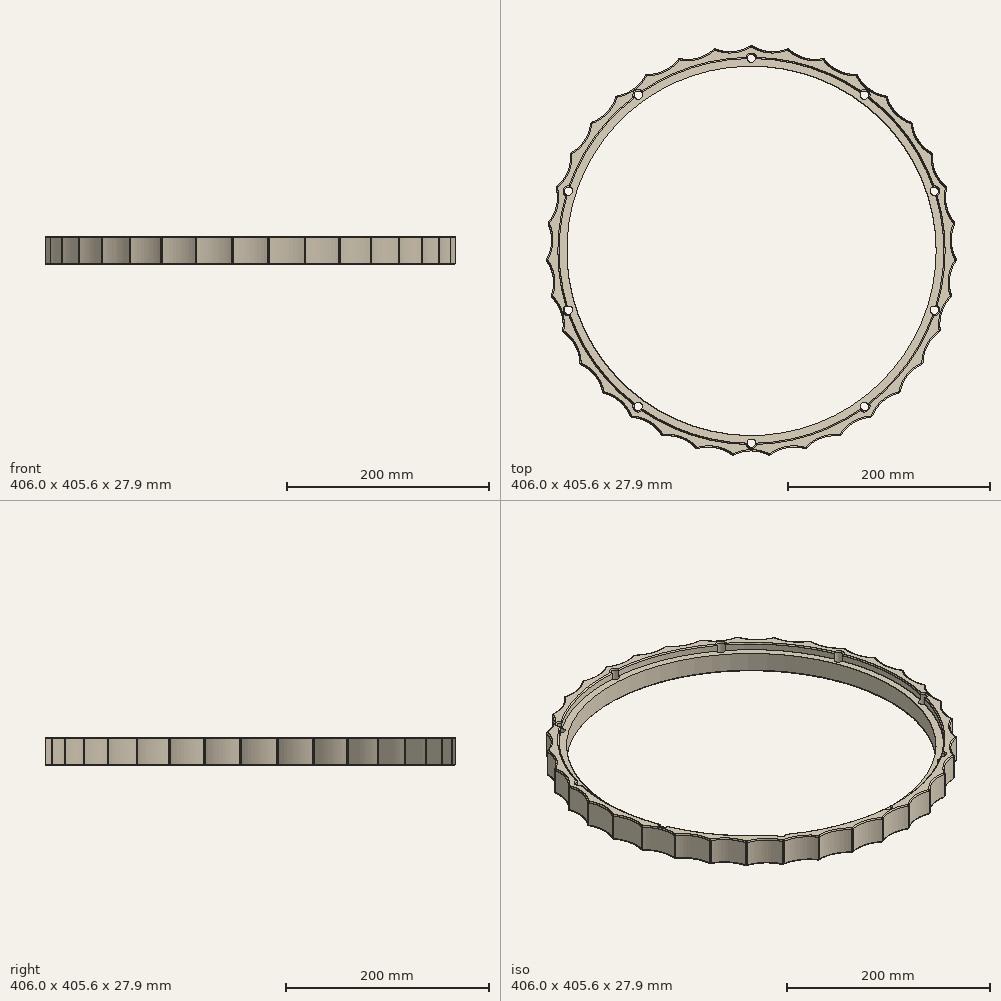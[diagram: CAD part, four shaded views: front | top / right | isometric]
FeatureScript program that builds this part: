
annotation { "Feature Type Name" : "Feature", "Feature Type Description" : "" }
export const myFeature = defineFeature(function(context is Context, id is Id, definition is map)
    precondition{}
    {
        {
            var Q0;
            Q0=qCreatedBy(makeId("Top.planeOp"),FACE);
            var sketch = newSketch(context, id + "F0", { "sketchPlane" : qUnion([Q0])});
            skCircle(sketch, "E0", {"center": v(0, 0) * mm, "radius": 182.88 * mm});
            skCircle(sketch, "E1", {"center": v(0, 0) * mm, "radius": 203.2 * mm});
            skSolve(sketch);
        }
        {
            var Q0;
            Q0=makeQuery(id+"F0.imprint","IMPRINT",FACE,{"disambiguationData":[TD([[makeQuery(id+"F0.imprint","IMPRINT",EDGE,{"derivedFrom":sQuery(id+"F0.wireOp",EDGE,"E0")}),-1.0]])]});
            extrude(context, id + "F1", {"entities" : qUnion([Q0]), "depth" : 27.94 * mm, "offsetDistance" : 25.4 * mm});
        }
        {
            var Q0;
            Q0=qCreatedBy(makeId("Top.planeOp"),FACE);
            var sketch = newSketch(context, id + "F2", { "sketchPlane" : qUnion([Q0])});
            skArc(sketch, "E2", {"start": v(-23.93, -265.87) * mm, "mid": v(0, -274.32) * mm, "end": v(23.93, -265.87) * mm});
            skArc(sketch, "E3.1.0", {"start": v(23.93, -265.87) * mm, "mid": v(48.98, -269.91) * mm, "end": v(71.02, -257.32) * mm});
            skArc(sketch, "E3.2.0", {"start": v(71.02, -257.32) * mm, "mid": v(96.39, -256.83) * mm, "end": v(115.82, -240.5) * mm});
            skArc(sketch, "E3.3.0", {"start": v(115.82, -240.5) * mm, "mid": v(140.7, -235.49) * mm, "end": v(156.9, -215.96) * mm});
            skArc(sketch, "E3.4.0", {"start": v(156.9, -215.96) * mm, "mid": v(180.49, -206.58) * mm, "end": v(192.95, -184.47) * mm});
            skArc(sketch, "E3.5.0", {"start": v(192.95, -184.47) * mm, "mid": v(214.47, -171.04) * mm, "end": v(222.78, -147.06) * mm});
            skArc(sketch, "E3.6.0", {"start": v(222.78, -147.06) * mm, "mid": v(241.56, -130) * mm, "end": v(245.46, -104.92) * mm});
            skArc(sketch, "E3.7.0", {"start": v(245.46, -104.92) * mm, "mid": v(260.9, -84.77) * mm, "end": v(260.25, -59.4) * mm});
            skArc(sketch, "E3.8.0", {"start": v(260.25, -59.4) * mm, "mid": v(271.84, -36.82) * mm, "end": v(266.67, -11.98) * mm});
            skArc(sketch, "E3.9.0", {"start": v(201.75, 27.33) * mm, "mid": v(197.92, 8.89) * mm, "end": v(203.39, -9.13) * mm});
            skArc(sketch, "E3.10.0", {"start": v(193.63, 62.91) * mm, "mid": v(193.15, 44.09) * mm, "end": v(201.75, 27.33) * mm});
            skArc(sketch, "E3.11.0", {"start": v(179.28, 96.48) * mm, "mid": v(182.18, 77.87) * mm, "end": v(193.63, 62.91) * mm});
            skArc(sketch, "E3.12.0", {"start": v(235.07, 126.5) * mm, "mid": v(228.94, 151.12) * mm, "end": v(208.7, 166.44) * mm});
            skArc(sketch, "E3.13.0", {"start": v(208.7, 166.44) * mm, "mid": v(198.28, 189.57) * mm, "end": v(175.63, 201.03) * mm});
            skArc(sketch, "E3.14.0", {"start": v(104.42, 174.78) * mm, "mid": v(116.45, 160.28) * mm, "end": v(133.95, 153.32) * mm});
            skArc(sketch, "E3.15.0", {"start": v(136.91, 229.16) * mm, "mid": v(119.02, 247.15) * mm, "end": v(93.8, 249.92) * mm});
            skArc(sketch, "E3.16.0", {"start": v(93.8, 249.92) * mm, "mid": v(72.98, 264.43) * mm, "end": v(47.66, 262.65) * mm});
            skArc(sketch, "E3.17.0", {"start": v(47.66, 262.65) * mm, "mid": v(24.59, 273.22) * mm, "end": v(0, 266.94) * mm});
            skArc(sketch, "E3.18.0", {"start": v(-36.35, 200.32) * mm, "mid": v(-17.76, 197.32) * mm, "end": v(0, 203.6) * mm});
            skArc(sketch, "E3.19.0", {"start": v(-47.66, 262.65) * mm, "mid": v(-72.98, 264.43) * mm, "end": v(-93.8, 249.92) * mm});
            skArc(sketch, "E3.20.0", {"start": v(-104.42, 174.78) * mm, "mid": v(-85.96, 178.5) * mm, "end": v(-71.54, 190.61) * mm});
            skArc(sketch, "E3.21.0", {"start": v(-136.91, 229.16) * mm, "mid": v(-161.24, 221.93) * mm, "end": v(-175.63, 201.03) * mm});
            skArc(sketch, "E3.22.0", {"start": v(-175.63, 201.03) * mm, "mid": v(-198.28, 189.57) * mm, "end": v(-208.7, 166.44) * mm});
            skArc(sketch, "E3.23.0", {"start": v(-179.28, 96.48) * mm, "mid": v(-165.35, 109.14) * mm, "end": v(-159.18, 126.94) * mm});
            skArc(sketch, "E3.24.0", {"start": v(-193.63, 62.91) * mm, "mid": v(-182.18, 77.87) * mm, "end": v(-179.28, 96.48) * mm});
            skArc(sketch, "E3.25.0", {"start": v(-201.75, 27.33) * mm, "mid": v(-193.15, 44.09) * mm, "end": v(-193.63, 62.91) * mm});
            skArc(sketch, "E3.26.0", {"start": v(-203.39, -9.13) * mm, "mid": v(-197.92, 8.89) * mm, "end": v(-201.75, 27.33) * mm});
            skArc(sketch, "E3.27.0", {"start": v(-266.67, -11.98) * mm, "mid": v(-271.84, -36.82) * mm, "end": v(-260.25, -59.4) * mm});
            skArc(sketch, "E3.28.0", {"start": v(-260.25, -59.4) * mm, "mid": v(-260.9, -84.77) * mm, "end": v(-245.46, -104.92) * mm});
            skArc(sketch, "E3.29.0", {"start": v(-245.46, -104.92) * mm, "mid": v(-241.56, -130) * mm, "end": v(-222.78, -147.06) * mm});
            skArc(sketch, "E3.30.0", {"start": v(-222.78, -147.06) * mm, "mid": v(-214.47, -171.04) * mm, "end": v(-192.95, -184.47) * mm});
            skArc(sketch, "E3.31.0", {"start": v(-192.95, -184.47) * mm, "mid": v(-180.49, -206.58) * mm, "end": v(-156.9, -215.96) * mm});
            skArc(sketch, "E3.32.0", {"start": v(-156.9, -215.96) * mm, "mid": v(-140.7, -235.49) * mm, "end": v(-115.82, -240.5) * mm});
            skArc(sketch, "E3.33.0", {"start": v(-115.82, -240.5) * mm, "mid": v(-96.39, -256.83) * mm, "end": v(-71.02, -257.32) * mm});
            skArc(sketch, "E3.34.0", {"start": v(-71.02, -257.32) * mm, "mid": v(-48.98, -269.91) * mm, "end": v(-23.93, -265.87) * mm});
            skPoint(sketch, "E3.center", {"position": v(0, 0) * mm});
            skArc(sketch, "E4.trimOffspring", {"start": v(0, 266.94) * mm, "mid": v(-24.59, 273.22) * mm, "end": v(-47.66, 262.65) * mm});
            skArc(sketch, "E5.trimOffspring", {"start": v(36.35, 200.32) * mm, "mid": v(52.7, 190.98) * mm, "end": v(71.54, 190.61) * mm});
            skArc(sketch, "E6.trimOffspring", {"start": v(0, 203.6) * mm, "mid": v(17.76, 197.32) * mm, "end": v(36.35, 200.32) * mm});
            skArc(sketch, "E7.trimOffspring", {"start": v(71.54, 190.61) * mm, "mid": v(85.96, 178.5) * mm, "end": v(104.42, 174.78) * mm});
            skArc(sketch, "E8.trimOffspring", {"start": v(-133.95, 153.32) * mm, "mid": v(-116.45, 160.28) * mm, "end": v(-104.42, 174.78) * mm});
            skArc(sketch, "E9.trimOffspring", {"start": v(-71.54, 190.61) * mm, "mid": v(-52.7, 190.98) * mm, "end": v(-36.35, 200.32) * mm});
            skArc(sketch, "E10.trimOffspring", {"start": v(-93.8, 249.92) * mm, "mid": v(-119.02, 247.15) * mm, "end": v(-136.91, 229.16) * mm});
            skArc(sketch, "E11.trimOffspring", {"start": v(253.88, 82.49) * mm, "mid": v(252.24, 107.81) * mm, "end": v(235.07, 126.5) * mm});
            skArc(sketch, "E12.trimOffspring", {"start": v(159.18, 126.94) * mm, "mid": v(165.35, 109.14) * mm, "end": v(179.28, 96.48) * mm});
            skArc(sketch, "E13.trimOffspring", {"start": v(175.63, 201.03) * mm, "mid": v(161.24, 221.93) * mm, "end": v(136.91, 229.16) * mm});
            skArc(sketch, "E14.trimOffspring", {"start": v(133.95, 153.32) * mm, "mid": v(143.2, 136.91) * mm, "end": v(159.18, 126.94) * mm});
            skArc(sketch, "E15.trimOffspring", {"start": v(-264.53, 35.83) * mm, "mid": v(-274.04, 12.3) * mm, "end": v(-266.67, -11.98) * mm});
            skArc(sketch, "E16.trimOffspring", {"start": v(-253.88, 82.49) * mm, "mid": v(-267.44, 61.04) * mm, "end": v(-264.53, 35.83) * mm});
            skArc(sketch, "E17.trimOffspring", {"start": v(-235.07, 126.5) * mm, "mid": v(-252.24, 107.81) * mm, "end": v(-253.88, 82.49) * mm});
            skArc(sketch, "E18.trimOffspring", {"start": v(-159.18, 126.94) * mm, "mid": v(-143.2, 136.91) * mm, "end": v(-133.95, 153.32) * mm});
            skArc(sketch, "E19.trimOffspring", {"start": v(-208.7, 166.44) * mm, "mid": v(-228.94, 151.12) * mm, "end": v(-235.07, 126.5) * mm});
            skArc(sketch, "E20.trimOffspring", {"start": v(-198.5, -45.3) * mm, "mid": v(-196.33, -26.6) * mm, "end": v(-203.39, -9.13) * mm});
            skArc(sketch, "E21.trimOffspring", {"start": v(-187.21, -80.02) * mm, "mid": v(-188.42, -61.22) * mm, "end": v(-198.5, -45.3) * mm});
            skArc(sketch, "E22.trimOffspring", {"start": v(-169.91, -112.16) * mm, "mid": v(-174.46, -93.88) * mm, "end": v(-187.21, -80.02) * mm});
            skArc(sketch, "E23.trimOffspring", {"start": v(-147.16, -140.7) * mm, "mid": v(-154.9, -123.53) * mm, "end": v(-169.91, -112.16) * mm});
            skArc(sketch, "E24.trimOffspring", {"start": v(-119.67, -164.71) * mm, "mid": v(-130.35, -149.2) * mm, "end": v(-147.16, -140.7) * mm});
            skArc(sketch, "E25.trimOffspring", {"start": v(-88.34, -183.43) * mm, "mid": v(-101.62, -170.08) * mm, "end": v(-119.67, -164.71) * mm});
            skArc(sketch, "E26.trimOffspring", {"start": v(-54.16, -196.26) * mm, "mid": v(-69.61, -185.49) * mm, "end": v(-88.34, -183.43) * mm});
            skArc(sketch, "E27.trimOffspring", {"start": v(-18.25, -202.78) * mm, "mid": v(-35.38, -194.94) * mm, "end": v(-54.16, -196.26) * mm});
            skArc(sketch, "E28.trimOffspring", {"start": v(18.25, -202.78) * mm, "mid": v(0, -198.12) * mm, "end": v(-18.25, -202.78) * mm});
            skArc(sketch, "E29.trimOffspring", {"start": v(54.16, -196.26) * mm, "mid": v(35.38, -194.94) * mm, "end": v(18.25, -202.78) * mm});
            skArc(sketch, "E30.trimOffspring", {"start": v(88.34, -183.43) * mm, "mid": v(69.61, -185.49) * mm, "end": v(54.16, -196.26) * mm});
            skArc(sketch, "E31.trimOffspring", {"start": v(119.67, -164.71) * mm, "mid": v(101.62, -170.08) * mm, "end": v(88.34, -183.43) * mm});
            skArc(sketch, "E32.trimOffspring", {"start": v(147.16, -140.7) * mm, "mid": v(130.35, -149.2) * mm, "end": v(119.67, -164.71) * mm});
            skArc(sketch, "E33.trimOffspring", {"start": v(169.91, -112.16) * mm, "mid": v(154.9, -123.53) * mm, "end": v(147.16, -140.7) * mm});
            skArc(sketch, "E34.trimOffspring", {"start": v(187.21, -80.02) * mm, "mid": v(174.46, -93.88) * mm, "end": v(169.91, -112.16) * mm});
            skArc(sketch, "E35.trimOffspring", {"start": v(198.5, -45.3) * mm, "mid": v(188.42, -61.22) * mm, "end": v(187.21, -80.02) * mm});
            skArc(sketch, "E36.trimOffspring", {"start": v(266.67, -11.98) * mm, "mid": v(274.04, 12.3) * mm, "end": v(264.53, 35.83) * mm});
            skArc(sketch, "E37.trimOffspring", {"start": v(203.39, -9.13) * mm, "mid": v(196.33, -26.6) * mm, "end": v(198.5, -45.3) * mm});
            skArc(sketch, "E38.trimOffspring", {"start": v(264.53, 35.83) * mm, "mid": v(267.44, 61.04) * mm, "end": v(253.88, 82.49) * mm});
            skSolve(sketch);
        }
        {
            var Q0;
            Q0=makeQuery(id+"F2.imprint","IMPRINT",FACE,{"disambiguationData":[TD([[makeQuery(id+"F2.imprint","IMPRINT",EDGE,{"derivedFrom":sQuery(id+"F2.wireOp",EDGE,"E2")}),1.0]])]});
            extrude(context, id + "F3", {"entities" : qUnion([Q0]), "operationType" : NewBodyOperationType.REMOVE, "depth" : 50.8 * mm, "offsetDistance" : 25.4 * mm});
        }
        {
            var Q0;
            Q0=qCreatedBy(makeId("Top.planeOp"),FACE);
            var sketch = newSketch(context, id + "F4", { "sketchPlane" : qUnion([Q0])});
            skPoint(sketch, "E39", {"position": v(0, 190.5) * mm});
            skPoint(sketch, "E40.1.0", {"position": v(-111.97, 154.12) * mm});
            skPoint(sketch, "E40.2.0", {"position": v(-181.18, 58.87) * mm});
            skPoint(sketch, "E40.3.0", {"position": v(-181.18, -58.87) * mm});
            skPoint(sketch, "E40.4.0", {"position": v(-111.97, -154.12) * mm});
            skPoint(sketch, "E40.5.0", {"position": v(0, -190.5) * mm});
            skPoint(sketch, "E40.6.0", {"position": v(111.97, -154.12) * mm});
            skPoint(sketch, "E40.7.0", {"position": v(181.18, -58.87) * mm});
            skPoint(sketch, "E40.8.0", {"position": v(181.18, 58.87) * mm});
            skPoint(sketch, "E40.9.0", {"position": v(111.97, 154.12) * mm});
            skPoint(sketch, "E40.center", {"position": v(0, 0) * mm});
            skSolve(sketch);
        }
        {
            var Q0;
            Q0=sQuery(id+"F4.wireOp",VERTEX,"E40.2.0");
            var Q1;
            Q1=sQuery(id+"F4.wireOp",VERTEX,"E40.3.0");
            var Q2;
            Q2=sQuery(id+"F4.wireOp",VERTEX,"E40.4.0");
            var Q3;
            Q3=sQuery(id+"F4.wireOp",VERTEX,"E40.5.0");
            var Q4;
            Q4=sQuery(id+"F4.wireOp",VERTEX,"E40.6.0");
            var Q5;
            Q5=sQuery(id+"F4.wireOp",VERTEX,"E40.7.0");
            var Q6;
            Q6=sQuery(id+"F4.wireOp",VERTEX,"E40.8.0");
            var Q7;
            Q7=sQuery(id+"F4.wireOp",VERTEX,"E40.9.0");
            var Q8;
            Q8=sQuery(id+"F4.wireOp",VERTEX,"E39");
            var Q9;
            Q9=sQuery(id+"F4.wireOp",VERTEX,"E40.1.0");
            var Q10;
            Q10=makeQuery(id+"F1.opExtrude","SWEPT_BODY",BODY,{"disambiguationData":[OSD([sQuery(id+"F0.wireOp",EDGE,"E0"),sQuery(id+"F0.wireOp",EDGE,"E1")])]});
            hole(context, id + "F5", {"style" : HoleStyle.C_BORE, "endStyle" : HoleEndStyle.BLIND, "oppositeDirection" : true, "holeDiameter" : 8.43 * mm, "cBoreDiameter" : 12.7 * mm, "cBoreDepth" : 10.16 * mm, "majorDiameter" : 25.4 * mm, "holeDepth" : 50.8 * mm, "isTappedThrough" : true, "tappedDepth" : 6.35 * mm, "tapClearance" : 3, "startFromSketch" : true, "locations" : qUnion([Q0, Q1, Q2, Q3, Q4, Q5, Q6, Q7, Q8, Q9]), "scope" : qUnion([Q10])});
        }
        {
            var Q0;
            Q0=qCreatedBy(makeId("Front.planeOp"),FACE);
            var sketch = newSketch(context, id + "F6", { "sketchPlane" : qUnion([Q0])});
            skLineSegment(sketch, "E41.bottom", {"start": v(190.5, 20.32) * mm, "end": v(165.1, 20.32) * mm});
            skLineSegment(sketch, "E41.top", {"start": v(190.5, 45.72) * mm, "end": v(165.1, 45.72) * mm});
            skLineSegment(sketch, "E41.left", {"start": v(190.5, 20.32) * mm, "end": v(190.5, 45.72) * mm});
            skLineSegment(sketch, "E41.right", {"start": v(165.1, 20.32) * mm, "end": v(165.1, 45.72) * mm});
            skLineSegment(sketch, "E42", {"start": v(0, 0) * mm, "end": v(0, -266.52) * mm, "construction": true});
            skSolve(sketch);
        }
        {
            var Q0;
            Q0=makeQuery(id+"F6.imprint","IMPRINT",FACE,{"disambiguationData":[TD([[makeQuery(id+"F6.imprint","IMPRINT",EDGE,{"derivedFrom":sQuery(id+"F6.wireOp",EDGE,"E41.bottom")}),-1.0]])]});
            var Q1;
            Q1=sQuery(id+"F6.wireOp",EDGE,"E42");
            revolve(context, id + "F7", {"operationType" : NewBodyOperationType.REMOVE, "surfaceOperationType" : NewSurfaceOperationType.NEW, "entities" : qUnion([Q0]), "axis" : qUnion([Q1]), "revolveType" : RevolveType.FULL, "oppositeDirection" : true});
        }
        {
            var Q0;
            Q0=makeQuery(id+"F3.boolean.opBoolean","COPY",FACE,{"derivedFrom":makeQuery(id+"F3.opExtrude","SWEPT_FACE",FACE,{"disambiguationData":[OSD([sQuery(id+"F2.wireOp",EDGE,"E3.24.0")])]})});
            var Q1;
            Q1=makeQuery(id+"F3.boolean.opBoolean","COPY",FACE,{"derivedFrom":makeQuery(id+"F3.opExtrude","SWEPT_FACE",FACE,{"disambiguationData":[OSD([sQuery(id+"F2.wireOp",EDGE,"E3.23.0")])]})});
            var Q2;
            Q2=makeQuery(id+"F3.boolean.opBoolean","COPY",FACE,{"derivedFrom":makeQuery(id+"F3.opExtrude","SWEPT_FACE",FACE,{"disambiguationData":[OSD([sQuery(id+"F2.wireOp",EDGE,"E18.trimOffspring")])]})});
            var Q3;
            Q3=makeQuery(id+"F3.boolean.opBoolean","COPY",FACE,{"derivedFrom":makeQuery(id+"F3.opExtrude","SWEPT_FACE",FACE,{"disambiguationData":[OSD([sQuery(id+"F2.wireOp",EDGE,"E8.trimOffspring")])]})});
            var Q4;
            Q4=makeQuery(id+"F3.boolean.opBoolean","COPY",FACE,{"derivedFrom":makeQuery(id+"F3.opExtrude","SWEPT_FACE",FACE,{"disambiguationData":[OSD([sQuery(id+"F2.wireOp",EDGE,"E3.20.0")])]})});
            var Q5;
            Q5=makeQuery(id+"F3.boolean.opBoolean","COPY",FACE,{"derivedFrom":makeQuery(id+"F3.opExtrude","SWEPT_FACE",FACE,{"disambiguationData":[OSD([sQuery(id+"F2.wireOp",EDGE,"E9.trimOffspring")])]})});
            var Q6;
            Q6=makeQuery(id+"F3.boolean.opBoolean","COPY",FACE,{"derivedFrom":makeQuery(id+"F3.opExtrude","SWEPT_FACE",FACE,{"disambiguationData":[OSD([sQuery(id+"F2.wireOp",EDGE,"E3.18.0")])]})});
            var Q7;
            Q7=makeQuery(id+"F3.boolean.opBoolean","COPY",FACE,{"derivedFrom":makeQuery(id+"F3.opExtrude","SWEPT_FACE",FACE,{"disambiguationData":[OSD([sQuery(id+"F2.wireOp",EDGE,"E6.trimOffspring")])]})});
            var Q8;
            Q8=makeQuery(id+"F3.boolean.opBoolean","COPY",FACE,{"derivedFrom":makeQuery(id+"F3.opExtrude","SWEPT_FACE",FACE,{"disambiguationData":[OSD([sQuery(id+"F2.wireOp",EDGE,"E5.trimOffspring")])]})});
            var Q9;
            Q9=makeQuery(id+"F3.boolean.opBoolean","COPY",FACE,{"derivedFrom":makeQuery(id+"F3.opExtrude","SWEPT_FACE",FACE,{"disambiguationData":[OSD([sQuery(id+"F2.wireOp",EDGE,"E7.trimOffspring")])]})});
            var Q10;
            Q10=makeQuery(id+"F3.boolean.opBoolean","COPY",FACE,{"derivedFrom":makeQuery(id+"F3.opExtrude","SWEPT_FACE",FACE,{"disambiguationData":[OSD([sQuery(id+"F2.wireOp",EDGE,"E3.14.0")])]})});
            var Q11;
            Q11=makeQuery(id+"F3.boolean.opBoolean","COPY",FACE,{"derivedFrom":makeQuery(id+"F3.opExtrude","SWEPT_FACE",FACE,{"disambiguationData":[OSD([sQuery(id+"F2.wireOp",EDGE,"E14.trimOffspring")])]})});
            var Q12;
            Q12=makeQuery(id+"F3.boolean.opBoolean","COPY",FACE,{"derivedFrom":makeQuery(id+"F3.opExtrude","SWEPT_FACE",FACE,{"disambiguationData":[OSD([sQuery(id+"F2.wireOp",EDGE,"E12.trimOffspring")])]})});
            var Q13;
            Q13=makeQuery(id+"F3.boolean.opBoolean","COPY",FACE,{"derivedFrom":makeQuery(id+"F3.opExtrude","SWEPT_FACE",FACE,{"disambiguationData":[OSD([sQuery(id+"F2.wireOp",EDGE,"E3.11.0")])]})});
            var Q14;
            Q14=makeQuery(id+"F3.boolean.opBoolean","COPY",FACE,{"derivedFrom":makeQuery(id+"F3.opExtrude","SWEPT_FACE",FACE,{"disambiguationData":[OSD([sQuery(id+"F2.wireOp",EDGE,"E28.trimOffspring")])]})});
            var Q15;
            Q15=makeQuery(id+"F3.boolean.opBoolean","COPY",FACE,{"derivedFrom":makeQuery(id+"F3.opExtrude","SWEPT_FACE",FACE,{"disambiguationData":[OSD([sQuery(id+"F2.wireOp",EDGE,"E29.trimOffspring")])]})});
            var Q16;
            Q16=makeQuery(id+"F3.boolean.opBoolean","COPY",FACE,{"derivedFrom":makeQuery(id+"F3.opExtrude","SWEPT_FACE",FACE,{"disambiguationData":[OSD([sQuery(id+"F2.wireOp",EDGE,"E30.trimOffspring")])]})});
            var Q17;
            Q17=makeQuery(id+"F3.boolean.opBoolean","COPY",FACE,{"derivedFrom":makeQuery(id+"F3.opExtrude","SWEPT_FACE",FACE,{"disambiguationData":[OSD([sQuery(id+"F2.wireOp",EDGE,"E32.trimOffspring")])]})});
            var Q18;
            Q18=makeQuery(id+"F3.boolean.opBoolean","COPY",FACE,{"derivedFrom":makeQuery(id+"F3.opExtrude","SWEPT_FACE",FACE,{"disambiguationData":[OSD([sQuery(id+"F2.wireOp",EDGE,"E33.trimOffspring")])]})});
            var Q19;
            Q19=makeQuery(id+"F3.boolean.opBoolean","COPY",FACE,{"derivedFrom":makeQuery(id+"F3.opExtrude","SWEPT_FACE",FACE,{"disambiguationData":[OSD([sQuery(id+"F2.wireOp",EDGE,"E34.trimOffspring")])]})});
            var Q20;
            Q20=makeQuery(id+"F3.boolean.opBoolean","COPY",FACE,{"derivedFrom":makeQuery(id+"F3.opExtrude","SWEPT_FACE",FACE,{"disambiguationData":[OSD([sQuery(id+"F2.wireOp",EDGE,"E31.trimOffspring")])]})});
            var Q21;
            Q21=makeQuery(id+"F3.boolean.opBoolean","COPY",FACE,{"derivedFrom":makeQuery(id+"F3.opExtrude","SWEPT_FACE",FACE,{"disambiguationData":[OSD([sQuery(id+"F2.wireOp",EDGE,"E35.trimOffspring")])]})});
            var Q22;
            Q22=makeQuery(id+"F3.boolean.opBoolean","COPY",FACE,{"derivedFrom":makeQuery(id+"F3.opExtrude","SWEPT_FACE",FACE,{"disambiguationData":[OSD([sQuery(id+"F2.wireOp",EDGE,"E37.trimOffspring")])]})});
            var Q23;
            Q23=makeQuery(id+"F3.boolean.opBoolean","COPY",FACE,{"derivedFrom":makeQuery(id+"F3.opExtrude","SWEPT_FACE",FACE,{"disambiguationData":[OSD([sQuery(id+"F2.wireOp",EDGE,"E3.9.0")])]})});
            var Q24;
            Q24=makeQuery(id+"F3.boolean.opBoolean","COPY",FACE,{"derivedFrom":makeQuery(id+"F3.opExtrude","SWEPT_FACE",FACE,{"disambiguationData":[OSD([sQuery(id+"F2.wireOp",EDGE,"E3.10.0")])]})});
            var Q25;
            Q25=makeQuery(id+"F3.boolean.opBoolean","COPY",FACE,{"derivedFrom":makeQuery(id+"F3.opExtrude","SWEPT_FACE",FACE,{"disambiguationData":[OSD([sQuery(id+"F2.wireOp",EDGE,"E3.25.0")])]})});
            var Q26;
            Q26=makeQuery(id+"F3.boolean.opBoolean","COPY",FACE,{"derivedFrom":makeQuery(id+"F3.opExtrude","SWEPT_FACE",FACE,{"disambiguationData":[OSD([sQuery(id+"F2.wireOp",EDGE,"E3.26.0")])]})});
            var Q27;
            Q27=makeQuery(id+"F3.boolean.opBoolean","COPY",FACE,{"derivedFrom":makeQuery(id+"F3.opExtrude","SWEPT_FACE",FACE,{"disambiguationData":[OSD([sQuery(id+"F2.wireOp",EDGE,"E20.trimOffspring")])]})});
            var Q28;
            Q28=makeQuery(id+"F3.boolean.opBoolean","COPY",FACE,{"derivedFrom":makeQuery(id+"F3.opExtrude","SWEPT_FACE",FACE,{"disambiguationData":[OSD([sQuery(id+"F2.wireOp",EDGE,"E21.trimOffspring")])]})});
            var Q29;
            Q29=makeQuery(id+"F3.boolean.opBoolean","COPY",FACE,{"derivedFrom":makeQuery(id+"F3.opExtrude","SWEPT_FACE",FACE,{"disambiguationData":[OSD([sQuery(id+"F2.wireOp",EDGE,"E22.trimOffspring")])]})});
            var Q30;
            Q30=makeQuery(id+"F3.boolean.opBoolean","COPY",FACE,{"derivedFrom":makeQuery(id+"F3.opExtrude","SWEPT_FACE",FACE,{"disambiguationData":[OSD([sQuery(id+"F2.wireOp",EDGE,"E23.trimOffspring")])]})});
            var Q31;
            Q31=makeQuery(id+"F3.boolean.opBoolean","COPY",FACE,{"derivedFrom":makeQuery(id+"F3.opExtrude","SWEPT_FACE",FACE,{"disambiguationData":[OSD([sQuery(id+"F2.wireOp",EDGE,"E24.trimOffspring")])]})});
            var Q32;
            Q32=makeQuery(id+"F3.boolean.opBoolean","COPY",FACE,{"derivedFrom":makeQuery(id+"F3.opExtrude","SWEPT_FACE",FACE,{"disambiguationData":[OSD([sQuery(id+"F2.wireOp",EDGE,"E25.trimOffspring")])]})});
            var Q33;
            Q33=makeQuery(id+"F3.boolean.opBoolean","COPY",FACE,{"derivedFrom":makeQuery(id+"F3.opExtrude","SWEPT_FACE",FACE,{"disambiguationData":[OSD([sQuery(id+"F2.wireOp",EDGE,"E26.trimOffspring")])]})});
            var Q34;
            Q34=makeQuery(id+"F3.boolean.opBoolean","COPY",FACE,{"derivedFrom":makeQuery(id+"F3.opExtrude","SWEPT_FACE",FACE,{"disambiguationData":[OSD([sQuery(id+"F2.wireOp",EDGE,"E27.trimOffspring")])]})});
            var Q35;
            Q35=makeQuery(id+"F1.opExtrude","CAP_FACE",FACE,{"disambiguationData":[OSD([sQuery(id+"F0.wireOp",EDGE,"E0"),sQuery(id+"F0.wireOp",EDGE,"E1")])],"isStart":false});
            var Q36;
            Q36=makeQuery(id+"F1.opExtrude","CAP_FACE",FACE,{"disambiguationData":[OSD([sQuery(id+"F0.wireOp",EDGE,"E0"),sQuery(id+"F0.wireOp",EDGE,"E1")])],"isStart":true});
            fillet(context, id + "F8", {"entities" : qUnion([Q0, Q1, Q2, Q3, Q4, Q5, Q6, Q7, Q8, Q9, Q10, Q11, Q12, Q13, Q14, Q15, Q16, Q17, Q18, Q19, Q20, Q21, Q22, Q23, Q24, Q25, Q26, Q27, Q28, Q29, Q30, Q31, Q32, Q33, Q34, Q35, Q36]), "tangentPropagation" : true, "radius" : 1.27 * mm, "defaultsChanged" : true, "vertexSettings" : [], "allowEdgeOverflow" : false});
        }
    });
